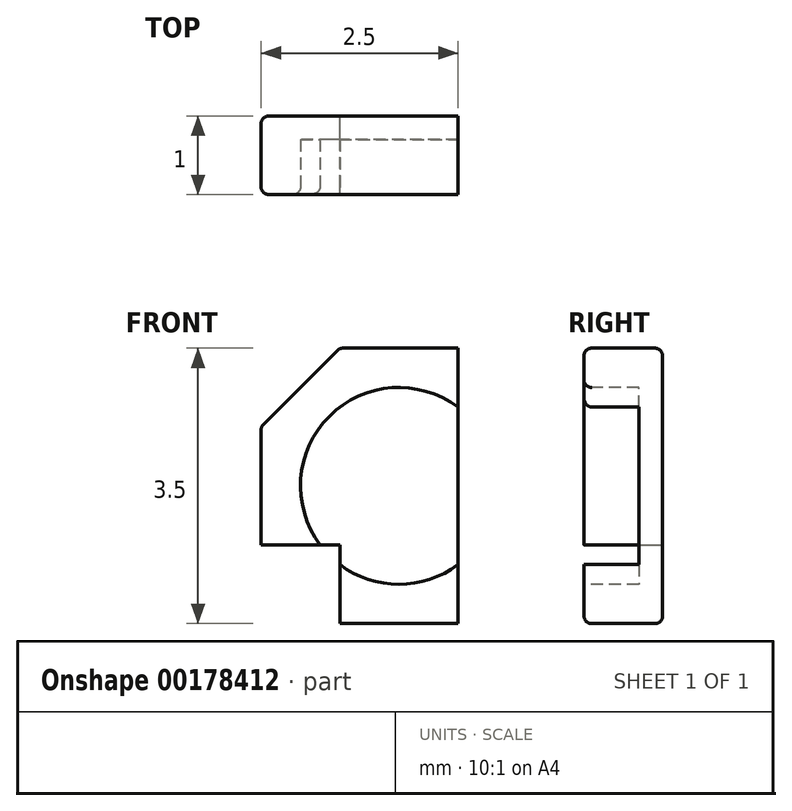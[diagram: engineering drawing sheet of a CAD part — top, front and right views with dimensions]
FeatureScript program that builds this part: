
annotation { "Feature Type Name" : "Feature", "Feature Type Description" : "" }
export const myFeature = defineFeature(function(context is Context, id is Id, definition is map)
    precondition{}
    {
        {
            var Q0;
            Q0=qCreatedBy(makeId("Front.planeOp"),FACE);
            var sketch = newSketch(context, id + "F0", { "sketchPlane" : qUnion([Q0])});
            skLineSegment(sketch, "E0.top", {"start": v(-0.75, -0.75) * mm, "end": v(-1.75, -0.75) * mm});
            skLineSegment(sketch, "E0.right", {"start": v(-1.75, 0.75) * mm, "end": v(-1.75, -0.75) * mm});
            skPoint(sketch, "E0.middle", {"position": v(0, 0) * mm});
            skLineSegment(sketch, "E1.bottom", {"start": v(0.75, 1.75) * mm, "end": v(-0.75, 1.75) * mm});
            skLineSegment(sketch, "E1.top", {"start": v(0.75, -1.75) * mm, "end": v(-0.75, -1.75) * mm});
            skLineSegment(sketch, "E1.left", {"start": v(0.75, 1.75) * mm, "end": v(0.75, -1.75) * mm});
            skLineSegment(sketch, "E1.right", {"start": v(-0.75, -0.75) * mm, "end": v(-0.75, -1.75) * mm});
            skLineSegment(sketch, "E2", {"start": v(-1.75, 0.75) * mm, "end": v(-0.75, 1.75) * mm});
            skPoint(sketch, "E0.left.end.orphan", {"position": v(1.75, -0.75) * mm});
            skPoint(sketch, "E0.bottom.start.orphan", {"position": v(1.75, 0.75) * mm});
            skArc(sketch, "E3", {"start": v(0.75, 1) * mm, "mid": v(-0.88, 0.88) * mm, "end": v(-1, -0.75) * mm});
            skArc(sketch, "E4.trimOffspring", {"start": v(-0.75, -1) * mm, "mid": v(0, -1.25) * mm, "end": v(0.75, -1) * mm});
            skSolve(sketch);
        }
        {
            var Q0;
            {var subQ3=sQuery(id+"F0.wireOp",EDGE,"E0.right");Q0=makeQuery(id+"F0.imprint","IMPRINT",FACE,{"disambiguationData":[TD([[makeQuery(id+"F0.imprint","IMPRINT",EDGE,{"derivedFrom":subQ3}),1.0]])]});}
            var Q1;
            {var subQ0=sQuery(id+"F0.wireOp",EDGE,"E1.top");Q1=makeQuery(id+"F0.imprint","IMPRINT",FACE,{"disambiguationData":[TD([[makeQuery(id+"F0.imprint","IMPRINT",EDGE,{"derivedFrom":subQ0}),-1.0]])]});}
            var Q2;
            {var subQ0=sQuery(id+"F0.wireOp",EDGE,"E3");Q2=makeQuery(id+"F0.imprint","IMPRINT",FACE,{"disambiguationData":[TD([[makeQuery(id+"F0.imprint","IMPRINT",EDGE,{"derivedFrom":subQ0}),1.0]])]});}
            extrude(context, id + "F1", {"entities" : qUnion([Q0, Q1, Q2]), "depth" : 1 * mm});
        }
        {
            var Q0;
            Q0=makeQuery(id+"F1.opExtrude","CAP_FACE",FACE,{"disambiguationData":[OSD([sQuery(id+"F0.wireOp",EDGE,"E0.top"),sQuery(id+"F0.wireOp",EDGE,"E0.right"),sQuery(id+"F0.wireOp",EDGE,"E1.bottom"),sQuery(id+"F0.wireOp",EDGE,"E1.top"),sQuery(id+"F0.wireOp",EDGE,"E1.left"),sQuery(id+"F0.wireOp",EDGE,"E1.right"),sQuery(id+"F0.wireOp",EDGE,"E2")])],"isStart":false});
            var sketch = newSketch(context, id + "F2", { "sketchPlane" : qUnion([Q0])});
            skCircle(sketch, "E5", {"center": v(0, 0) * mm, "radius": 1.25 * mm});
            skSolve(sketch);
        }
        {
            var Q0;
            {var subQ0=sQuery(id+"F2.wireOp",EDGE,"E5");var subQ1=makeQuery(id+"F1.opExtrude","CAP_EDGE",EDGE,{"disambiguationData":[OSD([sQuery(id+"F0.wireOp",EDGE,"E1.left")])],"isStart":false});var subQ2=makeQuery(id+"F2.imprint","INTERSECT",VERTEX,{"disambiguationData":[OD(0.0)],"derivedFrom":[subQ1,subQ0]});Q0=makeQuery(id+"F2.imprint","IMPRINT",FACE,{"disambiguationData":[TD([[makeQuery(id+"F2.imprint","IMPRINT",EDGE,{"disambiguationData":[TD([[subQ2,1.0]])],"derivedFrom":subQ0}),1.0]])]});}
            var Q1;
            {var subQ0=sQuery(id+"F2.wireOp",EDGE,"E5");var subQ1=makeQuery(id+"F1.opExtrude","CAP_EDGE",EDGE,{"disambiguationData":[OSD([sQuery(id+"F0.wireOp",EDGE,"E0.top")])],"isStart":false});var subQ2=makeQuery(id+"F2.imprint","INTERSECT",VERTEX,{"derivedFrom":[subQ1,subQ0]});Q1=makeQuery(id+"F2.imprint","IMPRINT",FACE,{"disambiguationData":[TD([[makeQuery(id+"F2.imprint","IMPRINT",EDGE,{"disambiguationData":[TD([[subQ2,-1.0]])],"derivedFrom":subQ0}),1.0]])]});}
            var Q2;
            {var subQ0=sQuery(id+"F2.wireOp",EDGE,"E5");var subQ5=makeQuery(id+"F1.opExtrude","CAP_EDGE",EDGE,{"disambiguationData":[OSD([sQuery(id+"F0.wireOp",EDGE,"E0.top")])],"isStart":false});var subQ7=makeQuery(id+"F2.imprint","INTERSECT",VERTEX,{"derivedFrom":[subQ5,subQ0]});Q2=makeQuery(id+"F2.imprint","IMPRINT",FACE,{"disambiguationData":[TD([[makeQuery(id+"F2.imprint","IMPRINT",EDGE,{"disambiguationData":[TD([[subQ7,1.0]])],"derivedFrom":subQ0}),1.0]])]});}
            extrude(context, id + "F3", {"entities" : qUnion([Q0, Q1, Q2]), "operationType" : NewBodyOperationType.REMOVE, "oppositeDirection" : true, "depth" : 0.7 * mm});
        }
        {
            var Q0;
            Q0=makeQuery(id+"F1.opExtrude","CAP_EDGE",EDGE,{"disambiguationData":[OSD([sQuery(id+"F0.wireOp",EDGE,"E1.bottom")])],"isStart":true});
            var Q1;
            Q1=makeQuery(id+"F1.opExtrude","CAP_EDGE",EDGE,{"disambiguationData":[OSD([sQuery(id+"F0.wireOp",EDGE,"E1.bottom")])],"isStart":false});
            var Q2;
            Q2=makeQuery(id+"F1.opExtrude","SWEPT_EDGE",EDGE,{"disambiguationData":[OSD([sQuery(id+"F0.wireOp",EDGE,"E1.bottom"),sQuery(id+"F0.wireOp",EDGE,"E2")])]});
            var Q3;
            {var subQ0=sQuery(id+"F0.wireOp",EDGE,"E0.top");var subQ1=sQuery(id+"F2.wireOp",EDGE,"E5");Q3=makeQuery(id+"F3.boolean.opBoolean","COPY",EDGE,{"disambiguationData":[TD([makeQuery(id+"F1.opExtrude","SWEPT_FACE",FACE,{"disambiguationData":[OSD([subQ0])]})])],"derivedFrom":makeQuery(id+"F3.opExtrude","CAP_EDGE",EDGE,{"disambiguationData":[OSD([subQ1])],"isStart":true})});}
            var Q4;
            {var subQ0=sQuery(id+"F0.wireOp",EDGE,"E1.right");var subQ2=sQuery(id+"F2.wireOp",EDGE,"E5");Q4=makeQuery(id+"F3.boolean.opBoolean","COPY",EDGE,{"disambiguationData":[TD([makeQuery(id+"F1.opExtrude","SWEPT_FACE",FACE,{"disambiguationData":[OSD([subQ0])]})])],"derivedFrom":makeQuery(id+"F3.opExtrude","CAP_EDGE",EDGE,{"disambiguationData":[OSD([subQ2])],"isStart":true})});}
            var Q5;
            Q5=makeQuery(id+"F1.opExtrude","CAP_EDGE",EDGE,{"disambiguationData":[OSD([sQuery(id+"F0.wireOp",EDGE,"E2")])],"isStart":false});
            var Q6;
            Q6=makeQuery(id+"F1.opExtrude","CAP_EDGE",EDGE,{"disambiguationData":[OSD([sQuery(id+"F0.wireOp",EDGE,"E2")])],"isStart":true});
            var Q7;
            Q7=makeQuery(id+"F1.opExtrude","CAP_EDGE",EDGE,{"disambiguationData":[OSD([sQuery(id+"F0.wireOp",EDGE,"E0.right")])],"isStart":false});
            var Q8;
            Q8=makeQuery(id+"F1.opExtrude","CAP_EDGE",EDGE,{"disambiguationData":[OSD([sQuery(id+"F0.wireOp",EDGE,"E0.right")])],"isStart":true});
            var Q9;
            Q9=makeQuery(id+"F1.opExtrude","SWEPT_EDGE",EDGE,{"disambiguationData":[OSD([sQuery(id+"F0.wireOp",EDGE,"E0.right"),sQuery(id+"F0.wireOp",EDGE,"E2")])]});
            var Q10;
            Q10=makeQuery(id+"F1.opExtrude","CAP_EDGE",EDGE,{"disambiguationData":[OSD([sQuery(id+"F0.wireOp",EDGE,"E1.top")])],"isStart":false});
            var Q11;
            Q11=makeQuery(id+"F1.opExtrude","CAP_EDGE",EDGE,{"disambiguationData":[OSD([sQuery(id+"F0.wireOp",EDGE,"E1.top")])],"isStart":true});
            fillet(context, id + "F4", {"entities" : qUnion([Q0, Q1, Q2, Q3, Q4, Q5, Q6, Q7, Q8, Q9, Q10, Q11]), "radius" : 0.1 * mm, "tangentPropagation" : true, "allowEdgeOverflow" : false});
        }
    });
